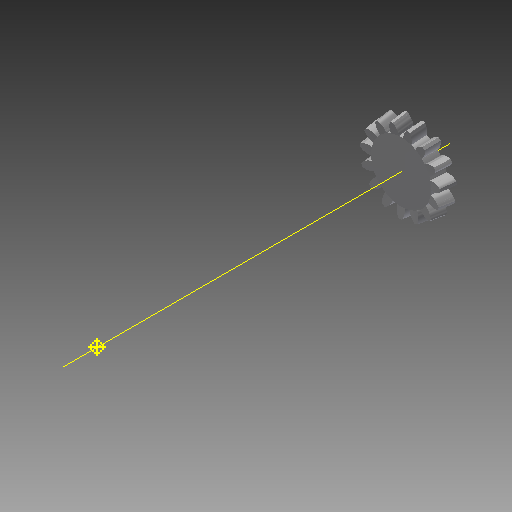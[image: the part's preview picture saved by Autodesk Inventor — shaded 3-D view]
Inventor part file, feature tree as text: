
AUTODESK INVENTOR PART (.ipt)
format: ipt  version: 2017 (Build 210142000, 142)  size: 501,248 bytes
history: native  units: mm
features: other x24, loft x2, pattern_circular x2, sketch x2
ambient origin geometry x6: Origin, XZ Plane, X Axis, Y Axis, Z Axis, Center Point
bodies: Solid1 (feature_tree)
feature tree (30):
  other  "Top Point"
  other  "Mesh Plane2"
  other  "Teeth Body"
  other  "Start Point"
  other  "Tooth Plane"
  other  "Start Sketch"
  other  "End Point"
  other  "3D Sketch Right"
  other  "End Plane Right"
  loft  "Loft Right"
  pattern_circular  "Circular Pattern Right"  [2 undecoded]
  other  "3D Sketch Left"
  other  "End Plane Left"
  loft  "Loft Left"
  pattern_circular  "Circular Pattern Left"  Angle=90.0deg  [1 undecoded]
  other  "Fix Body"
  sketch  "Sketch8"  dims[d2=42.954013mm d3=7.62mm d4=162.275585mm d5=90.0deg d7=7.250476mm d8=8.458821mm d9=15.799396mm d11=7.894581mm d12=6.908007mm d15=8.059277mm d16=15.053127mm d17=0.0mm d18=90.0deg d19=0.0mm d20=90.0deg d21=150.0mm d22=360.0deg d26=314.208686mm d27=7.840925mm d28=38.1mm d29=-1.166554mm d30=6.908007mm d31=8.059277mm d32=15.053127mm d35=0.0mm d37=0.0mm d39=0.0mm d40=90.0deg d41=150.0mm d42=360.0deg d46=90.0deg d47=90.0deg d48=0.0mm d49=0.0mm d50=90.0deg d51=2.094395mm d52=0.0mm d53=0.0mm d54=0.0mm d56=20.33796mm d57=23.271459mm d58=15.473366mm d59=22.172254mm d60=14.742497mm d61=22.172254mm d62=14.742497mm d63=90.0deg d64=90.0deg d65=314.208686mm d66=31.5mm d67=38.1mm d68=-1.166554mm d69=7.840925mm d70=8.059277mm d71=15.053127mm d72=6.908007mm d73=14.742497mm d74=22.172254mm d75=0.0mm d76=90.0deg d77=0.0mm d78=90.0deg d79=0.0mm d80=90.0deg d81=150.0mm d82=360.0deg d84=10.0mm d85=20.0mm d86=20.0mm d87=10.0mm d88=0.0mm d89=0.0mm]
  other  "Mesh Plane"
  other  "Top Plane"
  other  "Teeth Body Sketch"
  other  "End Plane"
  other  "End Sketch"
  other  "Helical Curve Left"
  other  "End Sketch Left"
  other  "Body Sketch"
  sketch  "Sketch6"  dims[d0=38.1mm d1=32.045432mm]
  other  "Srf1"
  other  "Helical Curve Right"
  other  "End Sketch Right"
  other  "Pitch Diameter"
note: 3 required parameter values undecoded (feature->parameter linkage not recoverable at this tier; creation-order binding heuristic only, values carry confidence <= 0.55)
